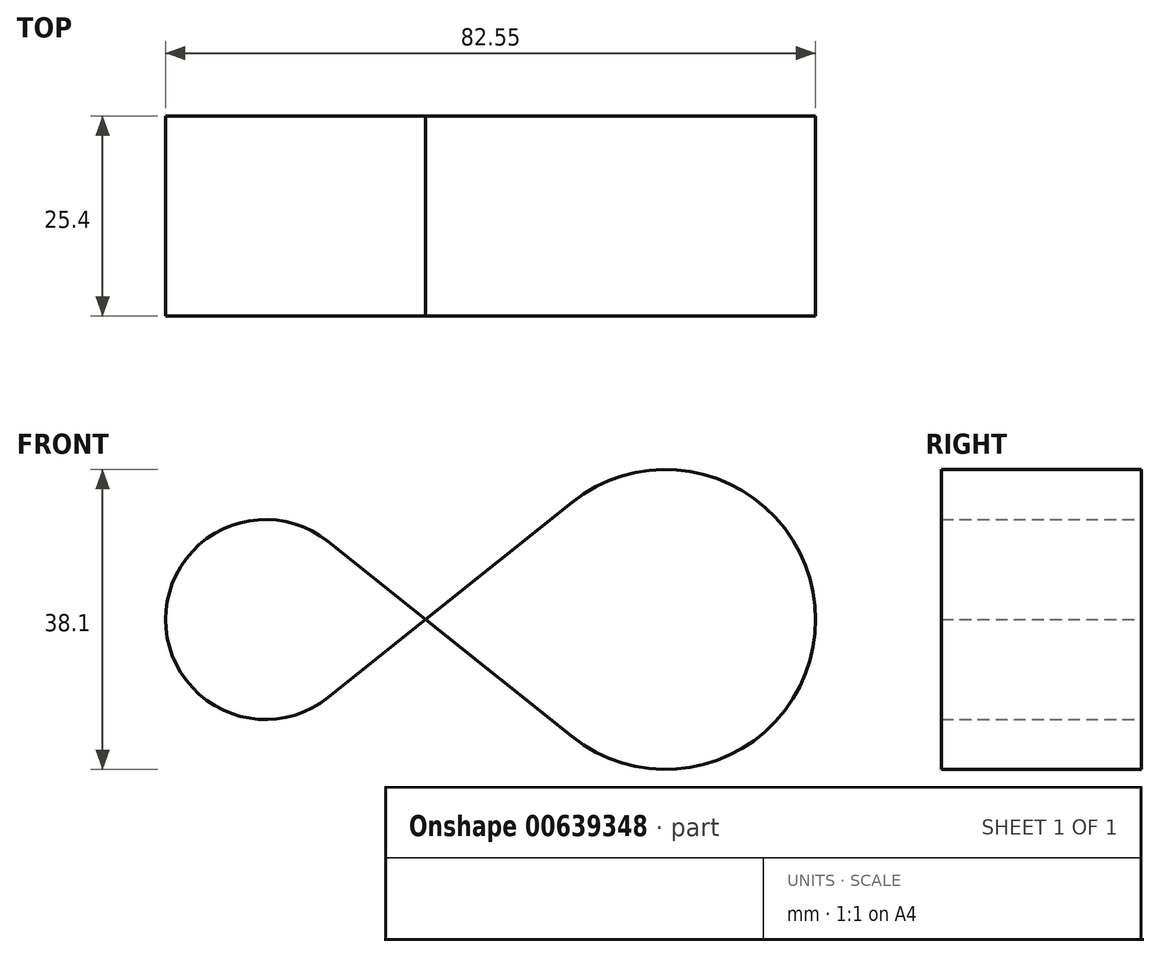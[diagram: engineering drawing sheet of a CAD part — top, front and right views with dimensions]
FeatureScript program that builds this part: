
annotation { "Feature Type Name" : "Feature", "Feature Type Description" : "" }
export const myFeature = defineFeature(function(context is Context, id is Id, definition is map)
    precondition{}
    {
        {
            var Q0;
            Q0=qCreatedBy(makeId("Front.planeOp"),FACE);
            var sketch = newSketch(context, id + "F0", { "sketchPlane" : qUnion([Q0])});
            skCircle(sketch, "E0", {"center": v(-25.8, 23.79) * mm, "radius": 12.7 * mm});
            skCircle(sketch, "E1", {"center": v(25, 23.79) * mm, "radius": 19.05 * mm});
            skLineSegment(sketch, "E2", {"start": v(-17.86, 13.87) * mm, "end": v(13.1, 38.66) * mm});
            skLineSegment(sketch, "E3", {"start": v(-25.8, 23.79) * mm, "end": v(-17.86, 13.87) * mm});
            skLineSegment(sketch, "E4", {"start": v(25, 23.79) * mm, "end": v(13.1, 38.66) * mm});
            skLineSegment(sketch, "E5", {"start": v(-25.8, 23.79) * mm, "end": v(25, 23.79) * mm});
            skLineSegment(sketch, "E6.MirrorCS", {"start": v(-17.86, 33.7) * mm, "end": v(13.1, 8.91) * mm});
            skLineSegment(sketch, "E7", {"start": v(13.1, 8.91) * mm, "end": v(25, 23.79) * mm});
            skLineSegment(sketch, "E8", {"start": v(-25.8, 23.79) * mm, "end": v(-17.86, 33.7) * mm});
            skPoint(sketch, "E9", {"position": v(25.08, 42.84) * mm});
            skPoint(sketch, "E10", {"position": v(43.32, 29.03) * mm});
            skLineSegment(sketch, "E11", {"start": v(18.73, 42.86) * mm, "end": v(31.43, 42.8) * mm});
            skPoint(sketch, "E12", {"position": v(32.96, 41.1) * mm});
            skLineSegment(sketch, "E13", {"start": v(27.19, 43.75) * mm, "end": v(38.73, 38.44) * mm});
            skPoint(sketch, "E14", {"position": v(29.2, 42.82) * mm});
            skArc(sketch, "E15", {"start": v(31.43, 42.8) * mm, "mid": v(31.38, 42.34) * mm, "end": v(31.23, 41.89) * mm});
            skPoint(sketch, "E16", {"position": v(-29.04, 36.06) * mm});
            skPoint(sketch, "E17", {"position": v(-35.46, 32.02) * mm});
            skLineSegment(sketch, "E18", {"start": v(-35.18, 34.44) * mm, "end": v(-22.9, 37.69) * mm});
            skLineSegment(sketch, "E19", {"start": v(-31.35, 36.85) * mm, "end": v(-39.58, 27.19) * mm});
            skArc(sketch, "E20", {"start": v(-35.18, 34.44) * mm, "mid": v(-34.9, 33.78) * mm, "end": v(-34.43, 33.24) * mm});
            skSolve(sketch);
        }
        {
            var Q0;
            {var subQ0=sQuery(id+"F0.wireOp",EDGE,"E4");Q0=makeQuery(id+"F0.imprint","IMPRINT",FACE,{"disambiguationData":[TD([[makeQuery(id+"F0.imprint","IMPRINT",EDGE,{"derivedFrom":subQ0}),-1.0]])]});}
            var Q1;
            {var subQ1=sQuery(id+"F0.wireOp",EDGE,"E1");var subQ3=sQuery(id+"F0.wireOp",EDGE,"E5");var subQ4=makeQuery(id+"F0.imprint","INTERSECT",VERTEX,{"derivedFrom":[subQ1,subQ3]});Q1=makeQuery(id+"F0.imprint","IMPRINT",FACE,{"disambiguationData":[TD([[makeQuery(id+"F0.imprint","IMPRINT",EDGE,{"disambiguationData":[TD([[subQ4,1.0]])],"derivedFrom":subQ1}),-1.0]])]});}
            var Q2;
            {var subQ0=sQuery(id+"F0.wireOp",EDGE,"E4");Q2=makeQuery(id+"F0.imprint","IMPRINT",FACE,{"disambiguationData":[TD([[makeQuery(id+"F0.imprint","IMPRINT",EDGE,{"derivedFrom":subQ0}),1.0]])]});}
            var Q3;
            {var subQ0=sQuery(id+"F0.wireOp",EDGE,"E7");Q3=makeQuery(id+"F0.imprint","IMPRINT",FACE,{"disambiguationData":[TD([[makeQuery(id+"F0.imprint","IMPRINT",EDGE,{"derivedFrom":subQ0}),1.0]])]});}
            var Q4;
            {var subQ1=sQuery(id+"F0.wireOp",EDGE,"E1");var subQ3=sQuery(id+"F0.wireOp",EDGE,"E5");var subQ4=makeQuery(id+"F0.imprint","INTERSECT",VERTEX,{"derivedFrom":[subQ1,subQ3]});Q4=makeQuery(id+"F0.imprint","IMPRINT",FACE,{"disambiguationData":[TD([[makeQuery(id+"F0.imprint","IMPRINT",EDGE,{"disambiguationData":[TD([[subQ4,-1.0]])],"derivedFrom":subQ1}),-1.0]])]});}
            var Q5;
            {var subQ1=sQuery(id+"F0.wireOp",EDGE,"E0");var subQ3=sQuery(id+"F0.wireOp",EDGE,"E5");var subQ4=makeQuery(id+"F0.imprint","INTERSECT",VERTEX,{"derivedFrom":[subQ1,subQ3]});Q5=makeQuery(id+"F0.imprint","IMPRINT",FACE,{"disambiguationData":[TD([[makeQuery(id+"F0.imprint","IMPRINT",EDGE,{"disambiguationData":[TD([[subQ4,-1.0]])],"derivedFrom":subQ1}),-1.0]])]});}
            var Q6;
            {var subQ0=sQuery(id+"F0.wireOp",EDGE,"E8");Q6=makeQuery(id+"F0.imprint","IMPRINT",FACE,{"disambiguationData":[TD([[makeQuery(id+"F0.imprint","IMPRINT",EDGE,{"derivedFrom":subQ0}),-1.0]])]});}
            var Q7;
            {var subQ1=sQuery(id+"F0.wireOp",EDGE,"E0");var subQ3=sQuery(id+"F0.wireOp",EDGE,"E5");var subQ4=makeQuery(id+"F0.imprint","INTERSECT",VERTEX,{"derivedFrom":[subQ1,subQ3]});Q7=makeQuery(id+"F0.imprint","IMPRINT",FACE,{"disambiguationData":[TD([[makeQuery(id+"F0.imprint","IMPRINT",EDGE,{"disambiguationData":[TD([[subQ4,1.0]])],"derivedFrom":subQ1}),-1.0]])]});}
            var Q8;
            {var subQ0=sQuery(id+"F0.wireOp",EDGE,"E3");Q8=makeQuery(id+"F0.imprint","IMPRINT",FACE,{"disambiguationData":[TD([[makeQuery(id+"F0.imprint","IMPRINT",EDGE,{"derivedFrom":subQ0}),-1.0]])]});}
            var Q9;
            {var subQ0=sQuery(id+"F0.wireOp",EDGE,"E3");Q9=makeQuery(id+"F0.imprint","IMPRINT",FACE,{"disambiguationData":[TD([[makeQuery(id+"F0.imprint","IMPRINT",EDGE,{"derivedFrom":subQ0}),1.0]])]});}
            extrude(context, id + "F1", {"entities" : qUnion([Q0, Q1, Q2, Q3, Q4, Q5, Q6, Q7, Q8, Q9]), "depth" : 25.4 * mm, "offsetDistance" : 25.4 * mm});
        }
    });
